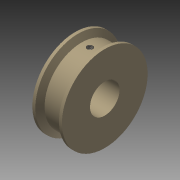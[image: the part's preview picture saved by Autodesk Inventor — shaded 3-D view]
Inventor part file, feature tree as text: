
AUTODESK INVENTOR PART (.ipt)
format: ipt  version: 2015 (Build 190159000, 159)  size: 120,320 bytes
history: native  units: mm
features: sketch x3, extrude x2, revolve x1, plane x1, thread x1
ambient origin geometry x8: Origin, YZ Plane, XZ Plane, XY Plane, X Axis, Y Axis, Z Axis, Center Point
bodies: 实体1 (feature_tree)
feature tree (8):
  revolve  "旋转1"  [1 undecoded]
  extrude  "拉伸1"  Depth=2.0mm
  plane  "工作平面1"
  extrude  "拉伸2"  TaperAngle=120.0deg  [1 undecoded]
  thread  "螺纹1"  [1 undecoded]
  sketch  "草图1"  dims[d1=29.0mm d2=4.0mm]
  sketch  "草图2"  dims[d4=20.0mm d5=2.0mm]
  sketch  "草图3"  dims[d6=120.0deg d7=120.0deg d8=2.0mm d9=90.0deg d10=20.0mm d11=10.0mm d12=0.0mm d13=4.0mm d14=10.0mm d15=0.0mm d16=10.0mm d17=0.0mm]
note: 3 required parameter values undecoded (feature->parameter linkage not recoverable at this tier; creation-order binding heuristic only, values carry confidence <= 0.55)